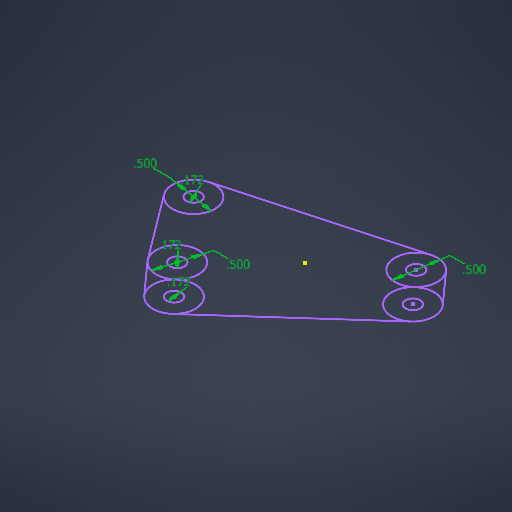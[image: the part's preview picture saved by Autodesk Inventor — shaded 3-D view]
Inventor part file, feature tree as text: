
AUTODESK INVENTOR PART (.ipt)
format: ipt  version: 2025.2 (Build 292293000, 293)  size: 194,560 bytes
history: native  units: in
note: dims shown in document units (in); Inventor stores cm internally (conversion verified against a paired STEP export)
features: sketch x1
ambient origin geometry x8: Origin, YZ Plane, XZ Plane, XY Plane, X Axis, Y Axis, Z Axis, Center Point
feature tree (1):
  sketch  "Sketch1"  dims[d0=0.172in d1=0.172in d2=0.172in d3=0.5in d4=0.5in d5=0.5in]
